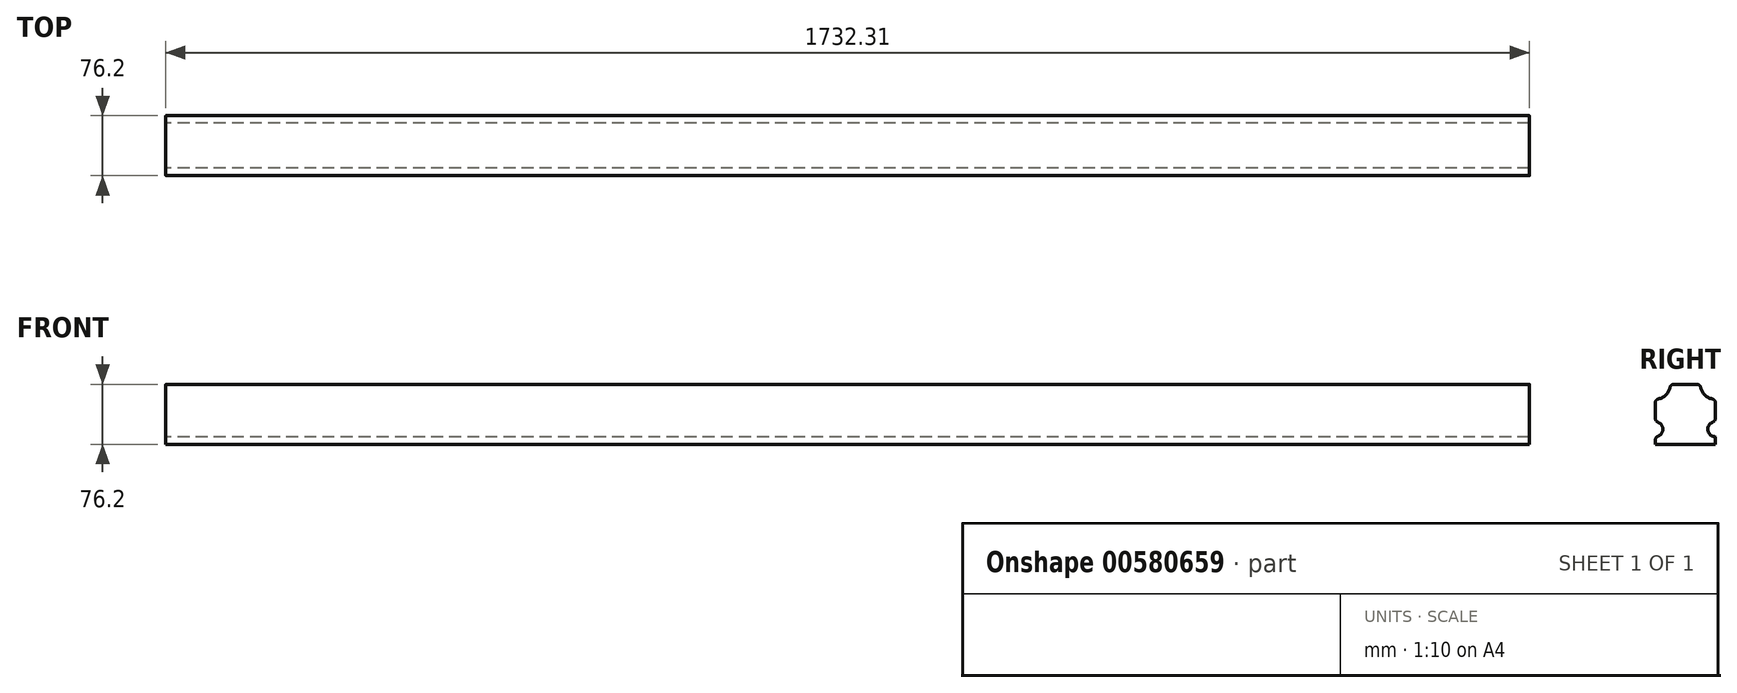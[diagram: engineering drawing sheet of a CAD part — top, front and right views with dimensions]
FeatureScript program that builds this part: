
annotation { "Feature Type Name" : "Feature", "Feature Type Description" : "" }
export const myFeature = defineFeature(function(context is Context, id is Id, definition is map)
    precondition{}
    {
        {
            var Q0;
            Q0=qCreatedBy(makeId("Right.planeOp"),FACE);
            var sketch = newSketch(context, id + "F0", { "sketchPlane" : qUnion([Q0])});
            skLineSegment(sketch, "E0.bottom", {"start": v(38.1, -38.1) * mm, "end": v(-38.1, -38.1) * mm});
            skLineSegment(sketch, "E0.top", {"start": v(19.05, 38.1) * mm, "end": v(-19.05, 38.1) * mm});
            skLineSegment(sketch, "E0.left", {"start": v(38.1, -38.1) * mm, "end": v(38.1, -28.58) * mm});
            skLineSegment(sketch, "E0.right", {"start": v(-38.1, -38.1) * mm, "end": v(-38.1, -28.58) * mm});
            skPoint(sketch, "E0.middle", {"position": v(0, 0) * mm});
            skArc(sketch, "E1", {"start": v(-38.1, 19.05) * mm, "mid": v(-24.63, 24.63) * mm, "end": v(-19.05, 38.1) * mm});
            skArc(sketch, "E2", {"start": v(19.05, 38.1) * mm, "mid": v(24.63, 24.63) * mm, "end": v(38.1, 19.05) * mm});
            skArc(sketch, "E3", {"start": v(-38.1, -28.58) * mm, "mid": v(-28.57, -19.05) * mm, "end": v(-38.1, -9.53) * mm});
            skArc(sketch, "E4", {"start": v(38.1, -9.53) * mm, "mid": v(28.58, -19.05) * mm, "end": v(38.1, -28.58) * mm});
            skLineSegment(sketch, "E5.trimOffspring", {"start": v(-38.1, -9.53) * mm, "end": v(-38.1, 19.05) * mm});
            skLineSegment(sketch, "E6.trimOffspring", {"start": v(38.1, -9.53) * mm, "end": v(38.1, 19.05) * mm});
            skSolve(sketch);
        }
        {
            var Q0;
            Q0=makeQuery(id+"F0.imprint","IMPRINT",FACE,{"disambiguationData":[TD([[makeQuery(id+"F0.imprint","IMPRINT",EDGE,{"derivedFrom":sQuery(id+"F0.wireOp",EDGE,"E0.bottom")}),-1.0]])]});
            extrude(context, id + "F1", {"entities" : qUnion([Q0]), "depth" : 1732.3 * mm, "offsetDistance" : 25.4 * mm});
        }
        {
            var Q0;
            Q0=makeQuery(id+"F1.opExtrude","SWEPT_EDGE",EDGE,{"disambiguationData":[OSD([sQuery(id+"F0.wireOp",EDGE,"E0.top"),sQuery(id+"F0.wireOp",EDGE,"E1")])]});
            var Q1;
            Q1=makeQuery(id+"F1.opExtrude","SWEPT_EDGE",EDGE,{"disambiguationData":[OSD([sQuery(id+"F0.wireOp",EDGE,"E2"),sQuery(id+"F0.wireOp",EDGE,"E6.trimOffspring")])]});
            var Q2;
            Q2=makeQuery(id+"F1.opExtrude","SWEPT_EDGE",EDGE,{"disambiguationData":[OSD([sQuery(id+"F0.wireOp",EDGE,"E1"),sQuery(id+"F0.wireOp",EDGE,"E5.trimOffspring")])]});
            var Q3;
            Q3=makeQuery(id+"F1.opExtrude","SWEPT_EDGE",EDGE,{"disambiguationData":[OSD([sQuery(id+"F0.wireOp",EDGE,"E3"),sQuery(id+"F0.wireOp",EDGE,"E5.trimOffspring")])]});
            var Q4;
            Q4=makeQuery(id+"F1.opExtrude","SWEPT_EDGE",EDGE,{"disambiguationData":[OSD([sQuery(id+"F0.wireOp",EDGE,"E0.right"),sQuery(id+"F0.wireOp",EDGE,"E3")])]});
            var Q5;
            Q5=makeQuery(id+"F1.opExtrude","SWEPT_EDGE",EDGE,{"disambiguationData":[OSD([sQuery(id+"F0.wireOp",EDGE,"E4"),sQuery(id+"F0.wireOp",EDGE,"E6.trimOffspring")])]});
            var Q6;
            Q6=makeQuery(id+"F1.opExtrude","SWEPT_EDGE",EDGE,{"disambiguationData":[OSD([sQuery(id+"F0.wireOp",EDGE,"E0.top"),sQuery(id+"F0.wireOp",EDGE,"E2")])]});
            fillet(context, id + "F2", {"entities" : qUnion([Q0, Q1, Q2, Q3, Q4, Q5, Q6]), "radius" : 5.08 * mm, "tangentPropagation" : true, "allowEdgeOverflow" : false});
        }
    });
